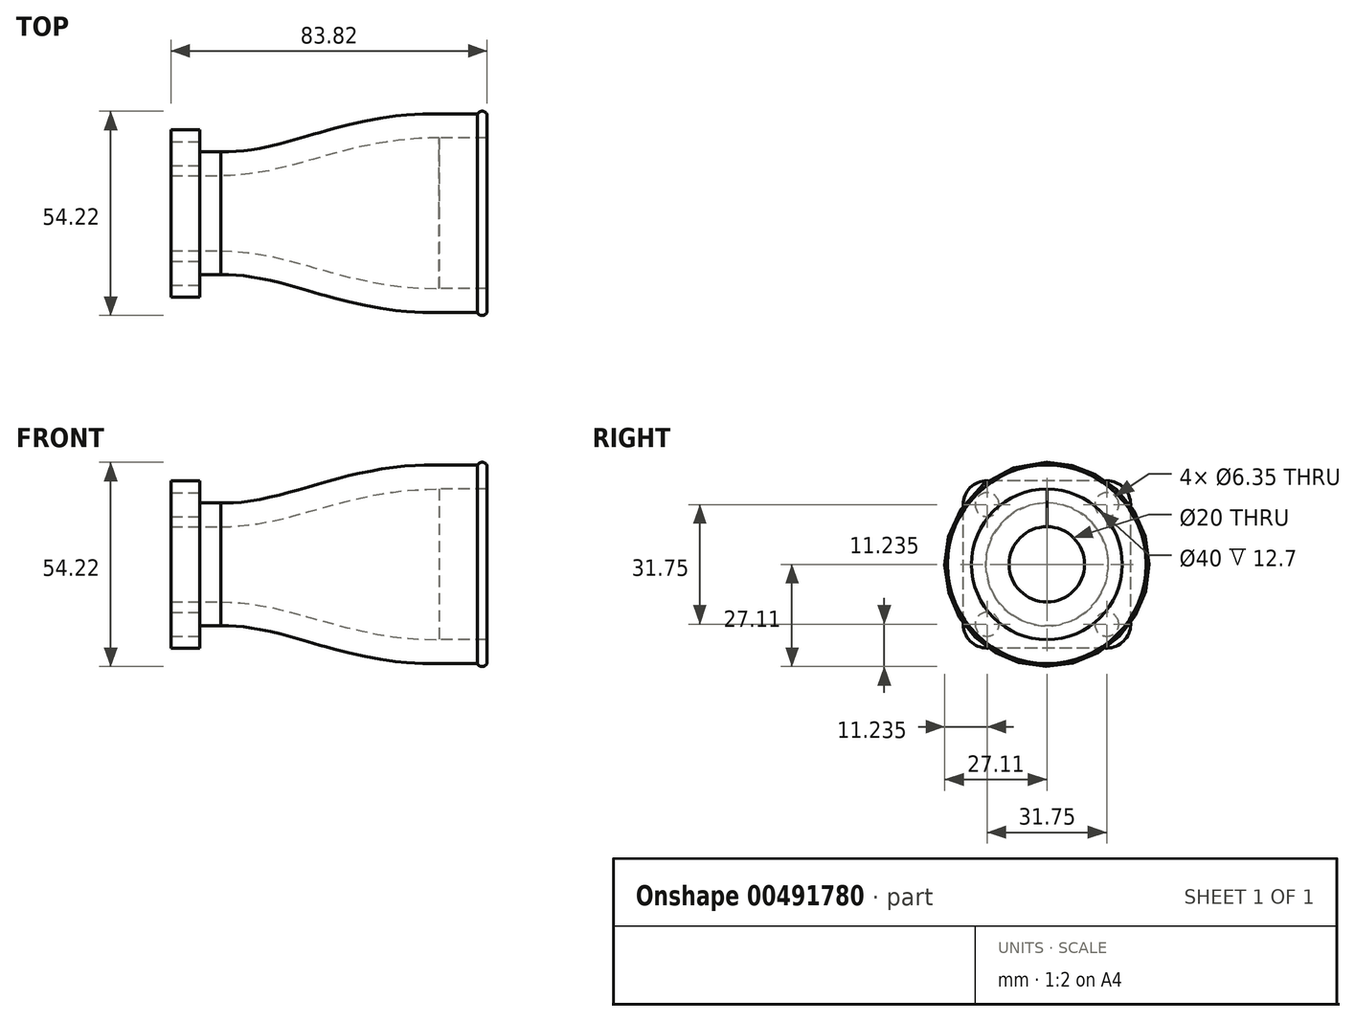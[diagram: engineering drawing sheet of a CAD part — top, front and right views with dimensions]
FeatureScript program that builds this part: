
annotation { "Feature Type Name" : "Feature", "Feature Type Description" : "" }
export const myFeature = defineFeature(function(context is Context, id is Id, definition is map)
    precondition{}
    {
        {
            var Q0;
            Q0=qCreatedBy(makeId("Right.planeOp"),FACE);
            var sketch = newSketch(context, id + "F0", { "sketchPlane" : qUnion([Q0])});
            skLineSegment(sketch, "E0.bottom", {"start": v(15.87, -22.23) * mm, "end": v(-15.87, -22.23) * mm});
            skLineSegment(sketch, "E0.top", {"start": v(15.87, 22.23) * mm, "end": v(-15.88, 22.22) * mm});
            skLineSegment(sketch, "E0.left", {"start": v(22.23, -15.88) * mm, "end": v(22.22, 15.88) * mm});
            skLineSegment(sketch, "E0.right", {"start": v(-22.22, -15.88) * mm, "end": v(-22.23, 15.88) * mm});
            skPoint(sketch, "E0.middle", {"position": v(0, 0) * mm});
            skPoint(sketch, "E1.visualSharp", {"position": v(-22.23, 22.22) * mm});
            skArc(sketch, "E1.filletArc", {"start": v(-15.88, 22.23) * mm, "mid": v(-20.37, 20.37) * mm, "end": v(-22.23, 15.87) * mm});
            skPoint(sketch, "E2.visualSharp", {"position": v(22.22, 22.23) * mm});
            skArc(sketch, "E2.filletArc", {"start": v(22.23, 15.88) * mm, "mid": v(20.37, 20.37) * mm, "end": v(15.87, 22.23) * mm});
            skPoint(sketch, "E3.visualSharp", {"position": v(22.23, -22.23) * mm});
            skArc(sketch, "E3.filletArc", {"start": v(15.87, -22.23) * mm, "mid": v(20.37, -20.37) * mm, "end": v(22.23, -15.88) * mm});
            skPoint(sketch, "E4.visualSharp", {"position": v(-22.22, -22.23) * mm});
            skArc(sketch, "E4.filletArc", {"start": v(-22.23, -15.88) * mm, "mid": v(-20.37, -20.37) * mm, "end": v(-15.87, -22.23) * mm});
            skCircle(sketch, "E5", {"center": v(-15.88, 15.87) * mm, "radius": 3.18 * mm});
            skCircle(sketch, "E6", {"center": v(15.87, 15.88) * mm, "radius": 3.18 * mm});
            skCircle(sketch, "E7", {"center": v(15.87, -15.88) * mm, "radius": 3.18 * mm});
            skCircle(sketch, "E8", {"center": v(-15.87, -15.88) * mm, "radius": 3.18 * mm});
            skCircle(sketch, "E9", {"center": v(0, 0) * mm, "radius": 10 * mm});
            skSolve(sketch);
        }
        {
            var Q0;
            Q0=makeQuery(id+"F0.imprint","IMPRINT",FACE,{"disambiguationData":[TD([[makeQuery(id+"F0.imprint","IMPRINT",EDGE,{"derivedFrom":sQuery(id+"F0.wireOp",EDGE,"E0.bottom")}),-1.0]])]});
            extrude(context, id + "F1", {"entities" : qUnion([Q0]), "oppositeDirection" : true, "depth" : 7.62 * mm});
        }
        {
            var Q0;
            Q0=qCreatedBy(makeId("Top.planeOp"),FACE);
            var sketch = newSketch(context, id + "F2", { "sketchPlane" : qUnion([Q0])});
            skLineSegment(sketch, "E10.0", {"start": v(0, 10) * mm, "end": v(0, -10) * mm});
            skLineSegment(sketch, "E11.0", {"start": v(0, 15.87) * mm, "end": v(0, -15.88) * mm});
            skPoint(sketch, "E12.0", {"position": v(-3.81, 22.22) * mm});
            skLineSegment(sketch, "E13.0", {"start": v(-7.62, 22.22) * mm, "end": v(0, 22.22) * mm});
            skLineSegment(sketch, "E14.0.0", {"start": v(0, 15.87) * mm, "end": v(0, 22.23) * mm});
            skLineSegment(sketch, "E14.0.1", {"start": v(0, 22.22) * mm, "end": v(-7.62, 22.22) * mm});
            skLineSegment(sketch, "E14.0.2", {"start": v(-7.62, 22.23) * mm, "end": v(-7.62, 15.87) * mm});
            skLineSegment(sketch, "E14.0.3", {"start": v(-7.62, 15.87) * mm, "end": v(0, 15.87) * mm});
            skLineSegment(sketch, "E15", {"start": v(0, 0) * mm, "end": v(63.5, 0) * mm, "construction": true});
            skLineSegment(sketch, "E16", {"start": v(63.5, 0) * mm, "end": v(63.5, 20) * mm, "construction": true});
            skLineSegment(sketch, "E17", {"start": v(25.4, 0) * mm, "end": v(25.4, 10) * mm, "construction": true});
            skLineSegment(sketch, "E18", {"start": v(38.1, 0) * mm, "end": v(38.1, 20) * mm, "construction": true});
            skLineSegment(sketch, "E19", {"start": v(0, 10) * mm, "end": v(0, 0) * mm, "construction": true});
            skFitSpline(sketch, "E20", {"points": [v(5.56, 10) * mm, v(63.5, 20) * mm], "startDerivative": vector(59.53, 0) * mm, "endDerivative": vector(76.2, 0) * mm});
            skFitSpline(sketch, "E21.0", {"points": [v(5.56, 16.35) * mm, v(7.77, 16.35) * mm, v(12, 16.63) * mm, v(18.07, 17.7) * mm, v(24.2, 19.24) * mm, v(30.63, 21.1) * mm, v(37.57, 23.03) * mm, v(45.22, 24.76) * mm, v(53.75, 26.02) * mm, v(60.12, 26.35) * mm, v(63.5, 26.35) * mm]});
            skLineSegment(sketch, "E22", {"start": v(0, 16.35) * mm, "end": v(0, 16.35) * mm});
            skLineSegment(sketch, "E23", {"start": v(63.5, 26.35) * mm, "end": v(63.5, 20) * mm});
            skLineSegment(sketch, "E24", {"start": v(0, 16.35) * mm, "end": v(5.56, 16.35) * mm});
            skLineSegment(sketch, "E25", {"start": v(5.56, 16.35) * mm, "end": v(5.56, 10) * mm, "construction": true});
            skLineSegment(sketch, "E26", {"start": v(5.56, 10) * mm, "end": v(0, 10) * mm});
            skSolve(sketch);
        }
        {
            var Q0;
            {var subQ1=sQuery(id+"F2.wireOp",EDGE,"E20");Q0=makeQuery(id+"F2.imprint","IMPRINT",FACE,{"disambiguationData":[TD([[makeQuery(id+"F2.imprint","IMPRINT",EDGE,{"derivedFrom":subQ1}),1.0]])]});}
            var Q1;
            Q1=sQuery(id+"F2.wireOp",EDGE,"E15");
            revolve(context, id + "F3", {"operationType" : NewBodyOperationType.ADD, "entities" : qUnion([Q0]), "axis" : qUnion([Q1]), "revolveType" : RevolveType.FULL});
        }
        {
            var Q0;
            Q0=makeQuery(id+"F3.opRevolve","SWEPT_FACE",FACE,{"disambiguationData":[OSD([sQuery(id+"F2.wireOp",EDGE,"E23")])]});
            extrude(context, id + "F4", {"entities" : qUnion([Q0]), "operationType" : NewBodyOperationType.ADD, "depth" : 12.7 * mm});
        }
        {
            var Q0;
            Q0=qCreatedBy(makeId("Top.planeOp"),FACE);
            var sketch = newSketch(context, id + "F5", { "sketchPlane" : qUnion([Q0])});
            skLineSegment(sketch, "E27", {"start": v(76.2, 26.35) * mm, "end": v(73.66, 26.35) * mm});
            skArc(sketch, "E28", {"start": v(76.2, 26.35) * mm, "mid": v(74.93, 27.11) * mm, "end": v(73.66, 26.35) * mm});
            skLineSegment(sketch, "E29", {"start": v(0, 0) * mm, "end": v(76.2, 0) * mm, "construction": true});
            skSolve(sketch);
        }
        {
            var Q0;
            Q0=makeQuery(id+"F5.imprint","IMPRINT",FACE,{"disambiguationData":[TD([[makeQuery(id+"F5.imprint","IMPRINT",EDGE,{"derivedFrom":sQuery(id+"F5.wireOp",EDGE,"E27")}),-1.0]])]});
            var Q1;
            Q1=sQuery(id+"F5.wireOp",EDGE,"E29");
            revolve(context, id + "F6", {"operationType" : NewBodyOperationType.ADD, "entities" : qUnion([Q0]), "axis" : qUnion([Q1]), "revolveType" : RevolveType.FULL});
        }
    });
